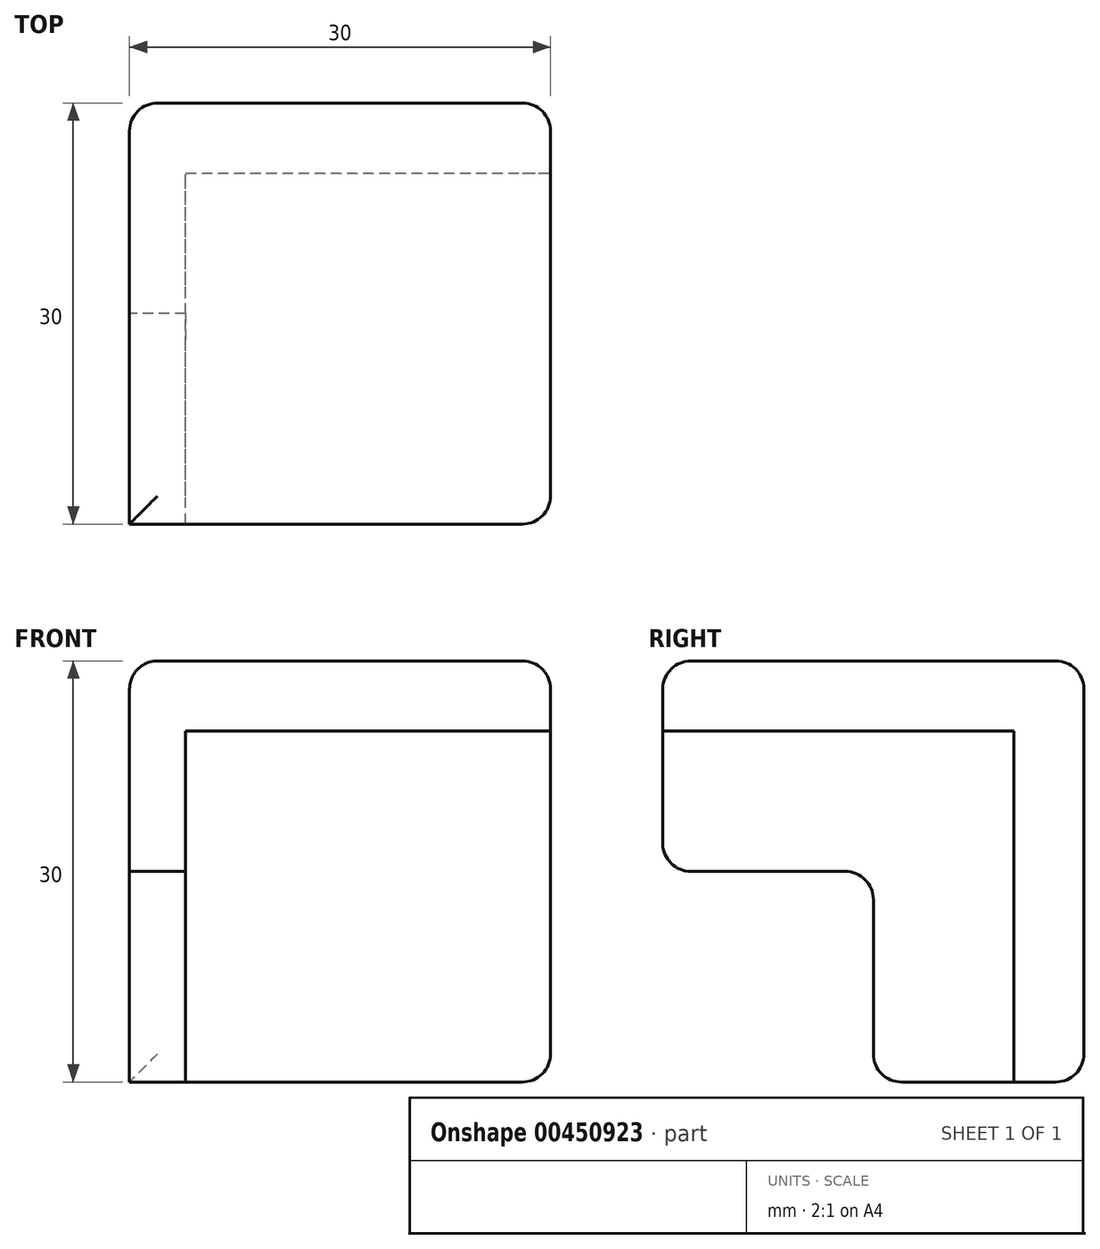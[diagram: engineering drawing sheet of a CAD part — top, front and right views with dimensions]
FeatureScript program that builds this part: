
annotation { "Feature Type Name" : "Feature", "Feature Type Description" : "" }
export const myFeature = defineFeature(function(context is Context, id is Id, definition is map)
    precondition{}
    {
        {
            var Q0;
            Q0=qCreatedBy(makeId("Right.planeOp"),FACE);
            var sketch = newSketch(context, id + "F0", { "sketchPlane" : qUnion([Q0])});
            skLineSegment(sketch, "E0", {"start": v(0, 0) * mm, "end": v(-30, 0) * mm});
            skLineSegment(sketch, "E1", {"start": v(-30, 0) * mm, "end": v(-30, -15) * mm});
            skLineSegment(sketch, "E2", {"start": v(-30, -15) * mm, "end": v(-15, -15) * mm});
            skLineSegment(sketch, "E3", {"start": v(-15, -15) * mm, "end": v(-15, -30) * mm});
            skLineSegment(sketch, "E4", {"start": v(-15, -30) * mm, "end": v(0, -30) * mm});
            skLineSegment(sketch, "E5", {"start": v(0, -30) * mm, "end": v(0, 0) * mm});
            skSolve(sketch);
        }
        {
            var Q0;
            Q0 = qSketchRegion(id + "F0", true);
            extrude(context, id + "F1", {"entities" : qUnion([Q0]), "depth" : 30 * mm});
        }
        {
            var Q0;
            Q0=makeQuery(id+"F1.opExtrude","CAP_FACE",FACE,{"disambiguationData":[OSD([sQuery(id+"F0.wireOp",EDGE,"E0"),sQuery(id+"F0.wireOp",EDGE,"E1"),sQuery(id+"F0.wireOp",EDGE,"E2"),sQuery(id+"F0.wireOp",EDGE,"E3"),sQuery(id+"F0.wireOp",EDGE,"E4"),sQuery(id+"F0.wireOp",EDGE,"E5")])],"isStart":false});
            var sketch = newSketch(context, id + "F2", { "sketchPlane" : qUnion([Q0])});
            skLineSegment(sketch, "E6", {"start": v(-30, -15) * mm, "end": v(-30, -5) * mm});
            skLineSegment(sketch, "E7", {"start": v(-30, -5) * mm, "end": v(-5, -5) * mm});
            skLineSegment(sketch, "E8", {"start": v(-5, -5) * mm, "end": v(-5, -30) * mm});
            skLineSegment(sketch, "E9", {"start": v(-5, -30) * mm, "end": v(-15, -30) * mm});
            skLineSegment(sketch, "E10", {"start": v(-15, -30) * mm, "end": v(-15, -15) * mm});
            skLineSegment(sketch, "E11", {"start": v(-15, -15) * mm, "end": v(-30, -15) * mm});
            skSolve(sketch);
        }
        {
            var Q0;
            Q0=makeQuery(id+"F2.imprint","IMPRINT",FACE,{"disambiguationData":[TD([[makeQuery(id+"F2.imprint","IMPRINT",EDGE,{"derivedFrom":sQuery(id+"F2.wireOp",EDGE,"E6")}),1.0]])]});
            extrude(context, id + "F3", {"entities" : qUnion([Q0]), "operationType" : NewBodyOperationType.REMOVE, "oppositeDirection" : true, "depth" : 26 * mm});
        }
        {
            var Q0;
            Q0=makeQuery(id+"F1.opExtrude","SWEPT_EDGE",EDGE,{"disambiguationData":[OSD([sQuery(id+"F0.wireOp",EDGE,"E0"),sQuery(id+"F0.wireOp",EDGE,"E1")])]});
            var Q1;
            Q1=makeQuery(id+"F1.opExtrude","SWEPT_EDGE",EDGE,{"disambiguationData":[OSD([sQuery(id+"F0.wireOp",EDGE,"E0"),sQuery(id+"F0.wireOp",EDGE,"E5")])]});
            var Q2;
            Q2=makeQuery(id+"F1.opExtrude","CAP_EDGE",EDGE,{"disambiguationData":[OSD([sQuery(id+"F0.wireOp",EDGE,"E0")])],"isStart":true});
            var Q3;
            Q3=makeQuery(id+"F1.opExtrude","CAP_EDGE",EDGE,{"disambiguationData":[OSD([sQuery(id+"F0.wireOp",EDGE,"E5")])],"isStart":true});
            var Q4;
            Q4=makeQuery(id+"F1.opExtrude","SWEPT_EDGE",EDGE,{"disambiguationData":[OSD([sQuery(id+"F0.wireOp",EDGE,"E4"),sQuery(id+"F0.wireOp",EDGE,"E5")])]});
            var Q5;
            Q5=makeQuery(id+"F1.opExtrude","CAP_EDGE",EDGE,{"disambiguationData":[OSD([sQuery(id+"F0.wireOp",EDGE,"E5")])],"isStart":false});
            var Q6;
            Q6=makeQuery(id+"F1.opExtrude","CAP_EDGE",EDGE,{"disambiguationData":[OSD([sQuery(id+"F0.wireOp",EDGE,"E0")])],"isStart":false});
            fillet(context, id + "F4", {"entities" : qUnion([Q0, Q1, Q2, Q3, Q4, Q5, Q6]), "radius" : 2 * mm, "tangentPropagation" : true, "allowEdgeOverflow" : false});
        }
        {
            var Q0;
            Q0=makeQuery(id+"F1.opExtrude","SWEPT_EDGE",EDGE,{"disambiguationData":[OSD([sQuery(id+"F0.wireOp",EDGE,"E3"),sQuery(id+"F0.wireOp",EDGE,"E4")])]});
            var Q1;
            Q1=makeQuery(id+"F1.opExtrude","SWEPT_EDGE",EDGE,{"disambiguationData":[OSD([sQuery(id+"F0.wireOp",EDGE,"E1"),sQuery(id+"F0.wireOp",EDGE,"E2")])]});
            var Q2;
            Q2=makeQuery(id+"F1.opExtrude","SWEPT_EDGE",EDGE,{"disambiguationData":[OSD([sQuery(id+"F0.wireOp",EDGE,"E2"),sQuery(id+"F0.wireOp",EDGE,"E3")])]});
            var Q3;
            Q3=makeQuery(id+"F1.opExtrude","CAP_EDGE",EDGE,{"disambiguationData":[OSD([sQuery(id+"F0.wireOp",EDGE,"E4")])],"isStart":false});
            var Q4;
            Q4=makeQuery(id+"F1.opExtrude","CAP_EDGE",EDGE,{"disambiguationData":[OSD([sQuery(id+"F0.wireOp",EDGE,"E1")])],"isStart":false});
            fillet(context, id + "F5", {"entities" : qUnion([Q0, Q1, Q2, Q3, Q4]), "radius" : 2 * mm, "tangentPropagation" : true, "allowEdgeOverflow" : false});
        }
    });
